# Revit family: Soap_Dispenser-Bradley_Corp-Deck_Mounted-Verge_Linea_6-3500
name_source: partatom
category: Specialty Equipment
revit_build: Autodesk Revit 2018 (Build: 20170223_1515(x64)
units: mm (PartAtom-declared; Revit-internal decimal feet)

## family parameters
Cut with Voids When Loaded = No
Host = Face
Part Type = Normal
Room Calculation Point = No
Round Connector Dimension = Use Diameter
Shared = No

## types (1)
- Verge Linea Series 6-3500
    ADA Compliant = Yes
    Assembly Code = C1030200
    Default Elevation = 48"
    Description = Touchless Deck Mounted Soap Dispenser -Verge Linea Series 6-3500, Paired with Crestt Series S53-3500 Faucet
    Manufacturer = Bradley Corporation
    Manufacturer Installation URL - English = https://www.bradleycorp.com
    Model = Verge Linea Series 6-3500
    Product Page URL = https://www.bradleycorp.com
    Product Tech Data URL - English = https://www.bradleycorp.com
    Specifications URL = https://www.bradleycorp.com
    Type Comments = Touchless Deck Mounted Soap Dispenser -Verge Crestt Series 6-3100, Paired with  Crestt Series S53-3100 Faucet
    Version = 1.0 - LOD200

## geometry (parser evidence)
native form markers: Sweep x2
no freeform markers — native parametric forms only
